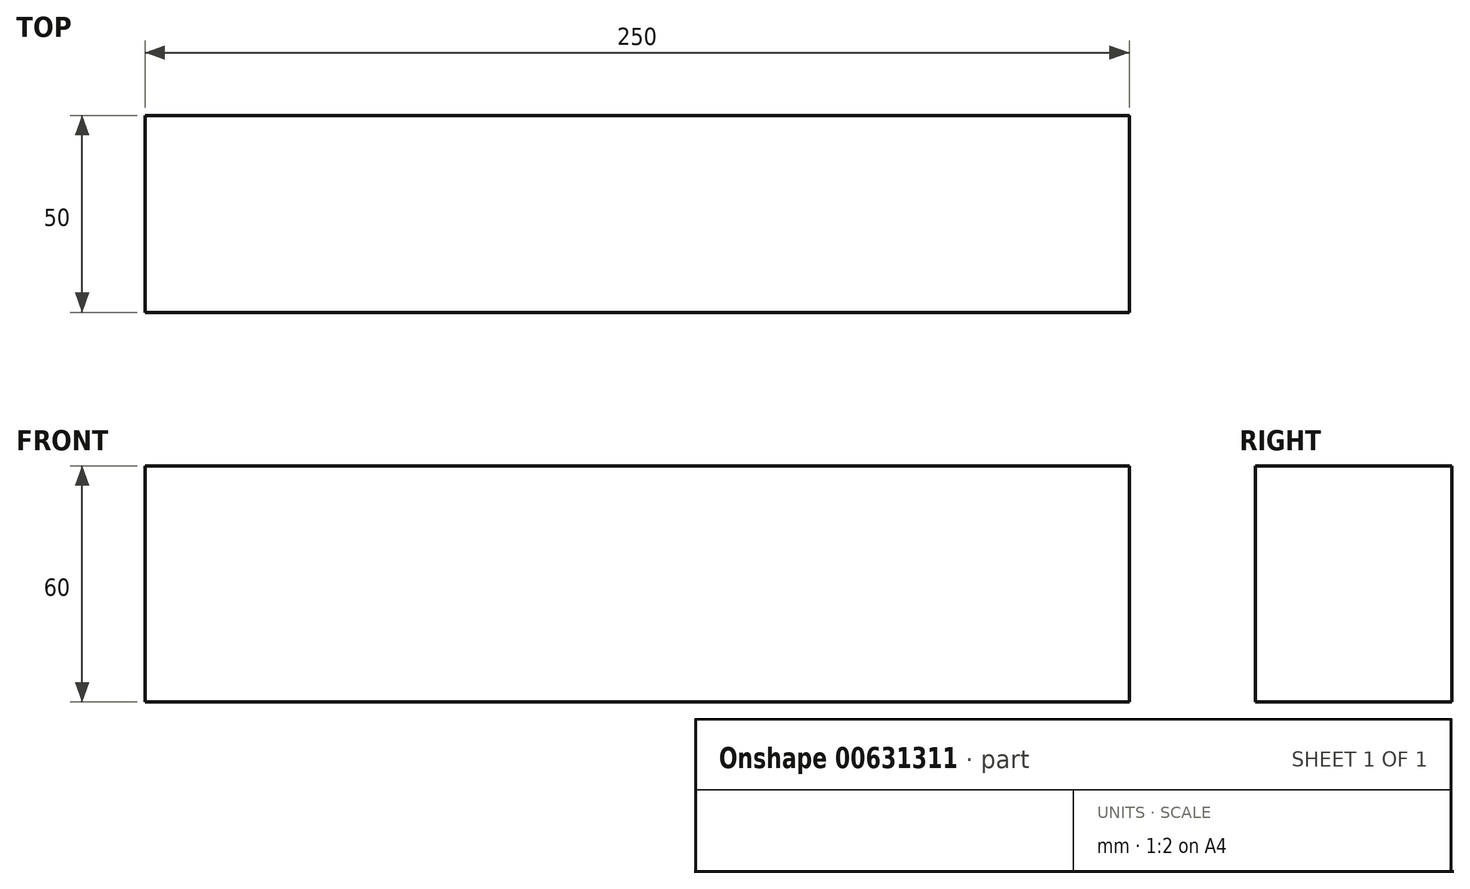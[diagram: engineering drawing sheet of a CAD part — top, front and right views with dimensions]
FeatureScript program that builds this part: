
annotation { "Feature Type Name" : "Feature", "Feature Type Description" : "" }
export const myFeature = defineFeature(function(context is Context, id is Id, definition is map)
    precondition{}
    {
        {
            var Q0;
            Q0=qCreatedBy(makeId("Front.planeOp"),FACE);
            var sketch = newSketch(context, id + "F0", { "sketchPlane" : qUnion([Q0])});
            skLineSegment(sketch, "E0.bottom", {"start": v(-125, 30) * mm, "end": v(125, 30) * mm});
            skLineSegment(sketch, "E0.top", {"start": v(-125, -30) * mm, "end": v(125, -30) * mm});
            skLineSegment(sketch, "E0.left", {"start": v(-125, 30) * mm, "end": v(-125, -30) * mm});
            skLineSegment(sketch, "E0.right", {"start": v(125, 30) * mm, "end": v(125, -30) * mm});
            skPoint(sketch, "E0.middle", {"position": v(0, 0) * mm});
            skSolve(sketch);
        }
        {
            var Q0;
            Q0=makeQuery(id+"F0.imprint","IMPRINT",FACE,{"disambiguationData":[TD([[makeQuery(id+"F0.imprint","IMPRINT",EDGE,{"derivedFrom":sQuery(id+"F0.wireOp",EDGE,"E0.bottom")}),-1.0]])]});
            extrude(context, id + "F1", {"entities" : qUnion([Q0]), "depth" : 50 * mm, "offsetDistance" : 25 * mm});
        }
    });
